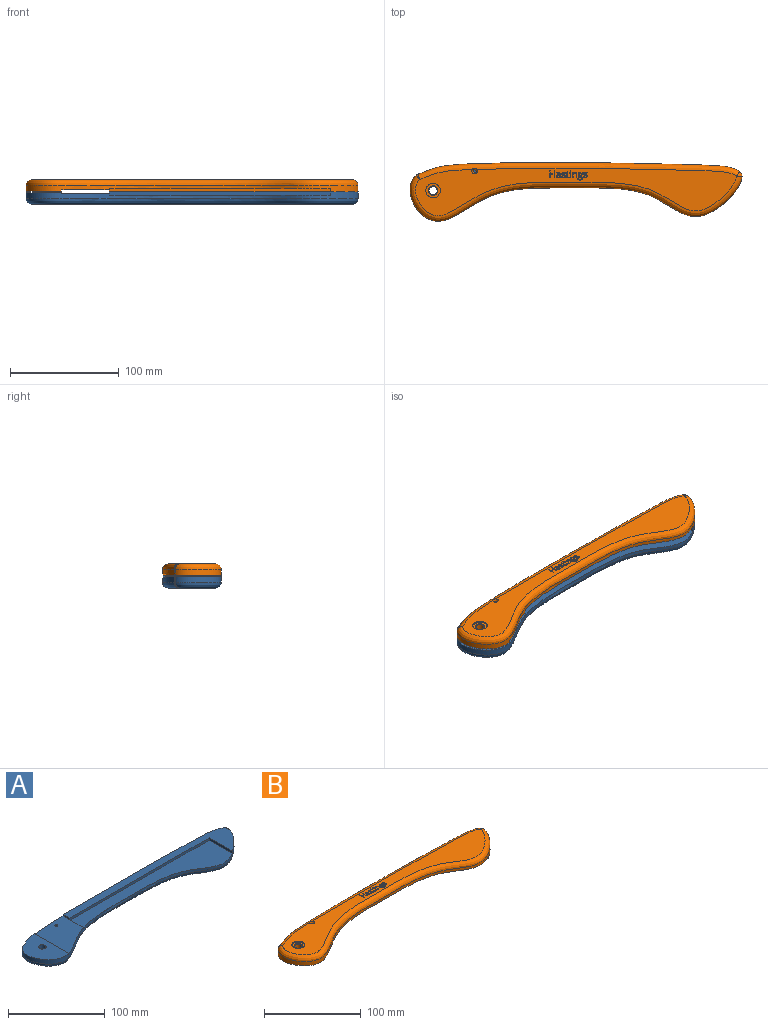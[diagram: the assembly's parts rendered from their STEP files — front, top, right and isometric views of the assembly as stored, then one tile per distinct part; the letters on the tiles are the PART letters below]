
ASSEMBLY  parts=2 mates=1
PART A: 28 faces, bbox 307.7x57.5x11.3 mm
  f0: cylinder r=3.81mm len=8.73mm, axis (0,0,-1), area 208.9mm2, adj f13,f26
  f1: cylinder r=5.08mm len=5.55mm, axis (0,0,-1), area 10.4mm2, adj f3,f6,f20,f26
  f2: cylinder r=1.52mm len=6.96mm, axis (0,0,-1), area 66.6mm2, adj f14,f25
  f3: extruded ~296.04x10.8mm, area 1751.2mm2, adj f1,f19,f22,f23,f24,f25,f26,f27
  f4: plane 19.58x1.24mm, normal (1,0,0), area 24.3mm2, adj f6,f15,f17,f25
  f5: plane 295.22x43.83mm, normal (0,0,-1), area 6249.9mm2, adj f7,f8,f9,f10,f11,f12,f14,f18
  f6: extruded ~305.25x42.05mm, area 1497.7mm2, adj f1,f4,f15,f16,f18,f19,f24,f25
  f7: plane 5.72x3.3mm, normal (-0.5,0.87,0), area 12.6mm2, adj f5,f8,f12,f13
  f8: plane 6.6x1.91mm, normal (-1,0,0), area 12.6mm2, adj f5,f7,f9,f13
  f9: plane 5.72x3.3mm, normal (-0.5,-0.87,0), area 12.6mm2, adj f5,f8,f10,f13
  f10: plane 5.72x3.3mm, normal (0.5,-0.87,0), area 12.6mm2, adj f5,f9,f11,f13
  f11: plane 6.6x1.91mm, normal (1,0,0), area 12.6mm2, adj f5,f10,f12,f13
  f12: plane 5.72x3.3mm, normal (0.5,0.87,0), area 12.6mm2, adj f5,f7,f11,f13
  f13: plane 13.2x11.43mm, normal (0,0,-1), area 67.5mm2, adj f0,f7,f8,f9,f10,f11,f12
  f14: cone r=2.54mm half-angle=21.8deg, axis (0,0,-1), area 34.9mm2, adj f2,f5,f22
  f15: plane 206.75x41.04mm, normal (0,0,1), area 3989.2mm2, adj f4,f6,f16,f17
  f16: plane 33.7x3.01mm, normal (-1,0,0), area 101.5mm2, adj f6,f15,f17,f27
  f17: plane 203.2x3.01mm, normal (0,-1,0), area 612.1mm2, adj f4,f15,f16,f23,f25,f27
  f18: bspline ~305.38x42.79mm, area 2862.2mm2, adj f5,f6,f20,f21
  f19: cylinder r=5.08mm len=6.19mm, axis (0,0,-1), area 31.9mm2, adj f3,f6,f21,f27
  f20: sphere r=5.08mm, area 9.5mm2, adj f1,f18,f22
  f21: sphere r=5.08mm, area 29.5mm2, adj f18,f19,f22
  f22: bspline ~296.04x15.55mm, area 2367.4mm2, adj f3,f5,f14,f20,f21
  f23: plane 9.75x1.77mm, normal (-1,0,0), area 17.3mm2, adj f3,f17,f25,f27
  f24: plane 49.96x1.14mm, normal (1,0,0), area 56.8mm2, adj f3,f6,f25,f26
  f25: plane 53.68x45.98mm, normal (0,0,1), area 1767.9mm2, adj f2,f3,f4,f6,f17,f23,f24
  f26: plane 52.52x34.33mm, normal (0,0,1), area 1250.7mm2, adj f0,f1,f3,f6,f24
  f27: plane 234.95x47.73mm, normal (0,0,1), area 2646.9mm2, adj f3,f6,f16,f17,f19,f23
PART B: 217 faces, bbox 307.7x57.5x11.1 mm
  f0: extruded ~296.04x10.8mm, area 1701.4mm2, adj f4,f5,f7,f17,f20,f21,f22,f216
  f1: extruded ~305.25x42.05mm, area 1469.7mm2, adj f2,f4,f7,f14,f15,f16,f20,f21
  f2: plane 33.7x2.85mm, normal (-1,0,0), area 96.2mm2, adj f1,f3,f14,f216
  f3: plane 203.2x2.85mm, normal (0,-1,0), area 579.7mm2, adj f2,f5,f14,f15,f21,f216
  f4: cylinder r=5.08mm len=6.03mm, axis (0,0,-1), area 31mm2, adj f0,f1,f19,f216
  f5: plane 9.75x1.81mm, normal (-1,0,0), area 17.6mm2, adj f0,f3,f21,f216
  f6: plane 295.22x43.83mm, normal (0,0,1), area 6146.7mm2, adj f10,f13,f16,f17,f23,f24,f25,f26
  f7: plane 49.96x1.15mm, normal (1,0,0), area 57.4mm2, adj f0,f1,f21,f22
  f8: cylinder r=3.81mm len=8.6mm, axis (0,0,-1), area 205.8mm2, adj f12,f22
  f9: cylinder r=1.52mm len=6.76mm, axis (0,0,-1), area 64.7mm2, adj f13,f21
  f10: cylinder r=6.64mm len=13.28mm, axis (0,0,1), area 56.2mm2, adj f6,f11
  f11: plane 13.28x13.28mm, normal (0,0,1), area 80mm2, adj f10,f12
  f12: cone r=3.81mm half-angle=45deg, axis (0,0,1), area 18.3mm2, adj f8,f11
  f13: cone r=1.52mm half-angle=21.8deg, axis (0,0,1), area 34.9mm2, adj f6,f9,f17
  f14: plane 206.75x41.04mm, normal (0,0,-1), area 3989.2mm2, adj f1,f2,f3,f15
  f15: plane 19.58x1.05mm, normal (1,0,0), area 20.5mm2, adj f1,f3,f14,f21
  f16: bspline ~305.38x42.79mm, area 2862.3mm2, adj f1,f6,f18,f19
  f17: bspline ~296.04x15.55mm, area 2367.3mm2, adj f0,f6,f13,f18,f19
  f18: sphere r=5.08mm, area 9.5mm2, adj f16,f17,f20
  f19: sphere r=5.08mm, area 29.5mm2, adj f4,f16,f17
  f20: cylinder r=5.08mm len=5.37mm, axis (0,0,-1), area 10mm2, adj f0,f1,f18,f22
  f21: plane 53.68x45.98mm, normal (0,0,-1), area 1767.9mm2, adj f0,f1,f3,f5,f7,f9,f15
  f22: plane 52.52x34.33mm, normal (0,0,-1), area 1250.7mm2, adj f0,f1,f7,f8,f20
  f23: extruded ~1.03x0.5mm, area 0.3mm2, adj f6,f24,f47,f48
  f24: extruded ~0.79x0.3mm, area 0.2mm2, adj f6,f23,f25,f48
  f25: extruded ~1.15x0.62mm, area 0.3mm2, adj f6,f24,f26,f48
  f26: extruded ~0.84x0.35mm, area 0.2mm2, adj f6,f25,f27,f48
  f27: extruded ~0.32x0.26mm, area 0.1mm2, adj f6,f26,f28,f48
  f28: extruded ~0.33x0.25mm, area 0.1mm2, adj f6,f27,f29,f48
  f29: extruded ~0.44x0.26mm, area 0.1mm2, adj f6,f28,f30,f48
  f30: extruded ~0.78x0.25mm, area 0.2mm2, adj f6,f29,f31,f48
  f31: extruded ~1.3x0.3mm, area 0.3mm2, adj f6,f30,f32,f48
  f32: plane 0.59x0.26mm, normal (-0.92,0.4,0), area 0.2mm2, adj f6,f31,f33,f48
  f33: extruded ~1.51x0.31mm, area 0.4mm2, adj f6,f32,f34,f48
  f34: extruded ~1.3x0.34mm, area 0.3mm2, adj f6,f33,f35,f48
  f35: extruded ~0.92x0.48mm, area 0.3mm2, adj f6,f34,f36,f48
  f36: extruded ~0.56x0.25mm, area 0.1mm2, adj f6,f35,f37,f48
  f37: extruded ~0.42x0.42mm, area 0.2mm2, adj f6,f36,f38,f48
  f38: extruded ~0.95x0.43mm, area 0.3mm2, adj f6,f37,f39,f48
  f39: extruded ~0.94x0.47mm, area 0.3mm2, adj f6,f38,f40,f48
  f40: extruded ~0.48x0.25mm, area 0.1mm2, adj f6,f39,f41,f48
  f41: extruded ~0.55x0.31mm, area 0.2mm2, adj f6,f40,f42,f48
  f42: extruded ~0.87x0.25mm, area 0.2mm2, adj f6,f41,f43,f48
  f43: extruded ~0.76x0.25mm, area 0.2mm2, adj f6,f42,f44,f48
  f44: extruded ~0.74x0.27mm, area 0.2mm2, adj f6,f43,f45,f48
  f45: plane 0.67x0.25mm, normal (1,0,0), area 0.2mm2, adj f6,f44,f46,f48
  f46: extruded ~1.48x0.3mm, area 0.4mm2, adj f6,f45,f47,f48
  f47: extruded ~1.4x0.36mm, area 0.4mm2, adj f6,f23,f46,f48
  f48: plane 4.95x3.39mm, normal (0,0,1), area 7mm2, adj f23,f24,f25,f26,f27,f28,f29,f30
  f49: extruded ~0.37x0.25mm, area 0.1mm2, adj f6,f50,f67,f68
  f50: extruded ~0.56x0.25mm, area 0.2mm2, adj f6,f49,f51,f68
  f51: extruded ~0.66x0.25mm, area 0.2mm2, adj f6,f50,f52,f68
  f52: plane 2.81x0.25mm, normal (-1,0,0), area 0.7mm2, adj f6,f51,f53,f68
  f53: plane 1.39x0.25mm, normal (0,1,0), area 0.4mm2, adj f6,f52,f54,f68
  f54: plane 0.56x0.25mm, normal (-1,0,0), area 0.1mm2, adj f6,f53,f55,f68
  f55: plane 1.39x0.25mm, normal (0,-1,0), area 0.4mm2, adj f6,f54,f56,f68
  f56: plane 1.11x0.25mm, normal (-1,0,0), area 0.3mm2, adj f6,f55,f57,f68
  f57: plane 0.42x0.25mm, normal (0,-1,0), area 0.1mm2, adj f6,f56,f58,f68
  f58: plane 1.02x0.3mm, normal (0.96,-0.29,0), area 0.3mm2, adj f6,f57,f59,f68
  f59: plane 0.69x0.3mm, normal (0.4,-0.92,0), area 0.2mm2, adj f6,f58,f60,f68
  f60: plane 0.35x0.25mm, normal (1,0,0), area 0.1mm2, adj f6,f59,f61,f68
  f61: plane 0.69x0.25mm, normal (0,1,0), area 0.2mm2, adj f6,f60,f62,f68
  f62: plane 2.84x0.25mm, normal (1,0,0), area 0.7mm2, adj f6,f61,f63,f68
  f63: extruded ~1.46x1.39mm, area 0.6mm2, adj f6,f62,f64,f68
  f64: extruded ~0.41x0.25mm, area 0.1mm2, adj f6,f63,f65,f68
  f65: extruded ~0.35x0.25mm, area 0.1mm2, adj f6,f64,f66,f68
  f66: plane 0.55x0.25mm, normal (-1,0,0), area 0.1mm2, adj f6,f65,f67,f68
  f67: extruded ~0.28x0.25mm, area 0.1mm2, adj f6,f49,f66,f68
  f68: plane 5.97x2.83mm, normal (0,0,1), area 5.9mm2, adj f49,f50,f51,f52,f53,f54,f55,f56
  f69: plane 0.72x0.25mm, normal (0,1,0), area 0.2mm2, adj f6,f70,f72,f73
  f70: plane 4.78x0.25mm, normal (-1,0,0), area 1.2mm2, adj f6,f69,f71,f73
  f71: plane 0.72x0.25mm, normal (0,-1,0), area 0.2mm2, adj f6,f70,f72,f73
  f72: plane 4.78x0.25mm, normal (1,0,0), area 1.2mm2, adj f6,f69,f71,f73
  f73: plane 4.78x0.72mm, normal (0,0,1), area 3.5mm2, adj f69,f70,f71,f72
  f74: extruded ~0.36x0.25mm, area 0.1mm2, adj f6,f75,f81,f82
  f75: extruded ~0.36x0.25mm, area 0.1mm2, adj f6,f74,f76,f82
  f76: extruded ~0.31x0.25mm, area 0.1mm2, adj f6,f75,f77,f82
  f77: extruded ~0.3x0.25mm, area 0.1mm2, adj f6,f76,f78,f82
  f78: extruded ~0.36x0.25mm, area 0.1mm2, adj f6,f77,f79,f82
  f79: extruded ~0.36x0.25mm, area 0.1mm2, adj f6,f78,f80,f82
  f80: extruded ~0.3x0.25mm, area 0.1mm2, adj f6,f79,f81,f82
  f81: extruded ~0.31x0.25mm, area 0.1mm2, adj f6,f74,f80,f82
  f82: plane 0.96x0.86mm, normal (0,0,1), area 0.7mm2, adj f74,f75,f76,f77,f78,f79,f80,f81
  f83: extruded ~0.76x0.28mm, area 0.2mm2, adj f84,f126,f127,f214
  f84: extruded ~0.82x0.28mm, area 0.2mm2, adj f83,f85,f127,f214
  f85: extruded ~0.79x0.27mm, area 0.2mm2, adj f84,f86,f127,f214
  f86: extruded ~1.08x1.07mm, area 0.4mm2, adj f85,f87,f127,f214
  f87: extruded ~1.06x1.03mm, area 0.4mm2, adj f86,f126,f127,f214
  f88: extruded ~0.59x0.33mm, area 0.2mm2, adj f89,f124,f127,f128
  f89: extruded ~0.68x0.28mm, area 0.2mm2, adj f88,f90,f127,f128
  f90: extruded ~0.77x0.25mm, area 0.2mm2, adj f89,f91,f127,f128
  f91: plane 0.87x0.25mm, normal (0,1,0), area 0.2mm2, adj f90,f92,f127,f128
  f92: extruded ~0.9x0.25mm, area 0.2mm2, adj f91,f93,f127,f128
  f93: extruded ~0.54x0.25mm, area 0.2mm2, adj f92,f94,f127,f128
  f94: extruded ~0.74x0.44mm, area 0.2mm2, adj f93,f95,f127,f128
  f95: extruded ~1.35x0.27mm, area 0.4mm2, adj f94,f124,f127,f128
  f96: plane 0.46x0.25mm, normal (-1,0,0), area 0.1mm2, adj f6,f97,f125,f127
  f97: plane 1.65x0.25mm, normal (0,-1,0), area 0.4mm2, adj f6,f96,f98,f127
  f98: extruded ~0.68x0.25mm, area 0.2mm2, adj f6,f97,f99,f127
  f99: extruded ~1.33x0.43mm, area 0.4mm2, adj f6,f98,f100,f127
  f100: extruded ~1.21x0.47mm, area 0.3mm2, adj f6,f99,f101,f127
  f101: extruded ~0.84x0.25mm, area 0.2mm2, adj f6,f100,f102,f127
  f102: extruded ~0.6x0.52mm, area 0.2mm2, adj f6,f101,f103,f127
  f103: extruded ~0.44x0.38mm, area 0.1mm2, adj f6,f102,f104,f127
  f104: extruded ~0.46x0.25mm, area 0.1mm2, adj f6,f103,f105,f127
  f105: extruded ~0.41x0.25mm, area 0.1mm2, adj f6,f104,f106,f127
  f106: extruded ~0.31x0.26mm, area 0.1mm2, adj f6,f105,f107,f127
  f107: extruded ~0.78x0.43mm, area 0.2mm2, adj f6,f106,f108,f127
  f108: extruded ~0.75x0.28mm, area 0.2mm2, adj f6,f107,f109,f127
  f109: extruded ~0.99x0.51mm, area 0.3mm2, adj f6,f108,f110,f127
  f110: extruded ~1.45x0.35mm, area 0.4mm2, adj f6,f109,f111,f127
  f111: extruded ~1.86x0.42mm, area 0.5mm2, adj f6,f110,f112,f127
  f112: extruded ~1.21x0.64mm, area 0.4mm2, adj f6,f111,f113,f127
  f113: extruded ~0.95x0.42mm, area 0.3mm2, adj f6,f112,f114,f127
  f114: extruded ~1.19x0.33mm, area 0.3mm2, adj f6,f113,f115,f127
  f115: plane 0.85x0.25mm, normal (0,-1,0), area 0.2mm2, adj f6,f114,f116,f127
  f116: extruded ~0.55x0.25mm, area 0.1mm2, adj f6,f115,f117,f127
  f117: extruded ~0.29x0.25mm, area 0.1mm2, adj f6,f116,f118,f127
  f118: extruded ~0.61x0.46mm, area 0.2mm2, adj f6,f117,f119,f127
  f119: extruded ~0.4x0.25mm, area 0.1mm2, adj f6,f118,f120,f127
  f120: extruded ~1.32x0.42mm, area 0.4mm2, adj f6,f119,f121,f127
  f121: extruded ~1.12x0.48mm, area 0.3mm2, adj f6,f120,f122,f127
  f122: extruded ~0.56x0.25mm, area 0.1mm2, adj f6,f121,f123,f127
  f123: extruded ~0.4x0.25mm, area 0.1mm2, adj f6,f122,f125,f127
  f124: extruded ~0.94x0.25mm, area 0.2mm2, adj f88,f95,f127,f128
  f125: plane 0.88x0.25mm, normal (-0.12,0.99,0), area 0.2mm2, adj f6,f96,f123,f127
  f126: extruded ~0.79x0.26mm, area 0.2mm2, adj f83,f87,f127,f214
  f127: plane 7.01x4.51mm, normal (0,0,1), area 13.1mm2, adj f83,f84,f85,f86,f87,f88,f89,f90
  f128: plane 3.05x1.7mm, normal (0,0,1), area 4.4mm2, adj f88,f89,f90,f91,f92,f93,f94,f95
  f129: extruded ~1.06x0.37mm, area 0.3mm2, adj f130,f155,f156,f215
  f130: extruded ~0.66x0.25mm, area 0.2mm2, adj f129,f131,f156,f215
  f131: extruded ~0.6x0.25mm, area 0.2mm2, adj f130,f132,f156,f215
  f132: extruded ~0.74x0.38mm, area 0.2mm2, adj f131,f133,f156,f215
  f133: extruded ~1.24x0.27mm, area 0.3mm2, adj f132,f134,f156,f215
  f134: plane 0.72x0.25mm, normal (-0.04,1,0), area 0.2mm2, adj f133,f135,f156,f215
  f135: plane 0.43x0.25mm, normal (1,0,0), area 0.1mm2, adj f134,f155,f156,f215
  f136: plane 0.68x0.25mm, normal (0.98,0.21,0), area 0.2mm2, adj f6,f137,f154,f156
  f137: plane 0.54x0.25mm, normal (0,1,0), area 0.1mm2, adj f6,f136,f138,f156
  f138: plane 3.26x0.25mm, normal (-1,0,0), area 0.8mm2, adj f6,f137,f139,f156
  f139: extruded ~1.22x0.41mm, area 0.3mm2, adj f6,f138,f140,f156
  f140: extruded ~1.27x0.38mm, area 0.3mm2, adj f6,f139,f141,f156
  f141: extruded ~0.84x0.25mm, area 0.2mm2, adj f6,f140,f142,f156
  f142: extruded ~0.77x0.3mm, area 0.2mm2, adj f6,f141,f143,f156
  f143: plane 0.55x0.25mm, normal (0.93,0.37,0), area 0.2mm2, adj f6,f142,f144,f156
  f144: extruded ~1.35x0.37mm, area 0.4mm2, adj f6,f143,f145,f156
  f145: extruded ~0.77x0.27mm, area 0.2mm2, adj f6,f144,f146,f156
  f146: extruded ~0.83x0.25mm, area 0.2mm2, adj f6,f145,f147,f156
  f147: plane 0.3x0.25mm, normal (1,0,0), area 0.1mm2, adj f6,f146,f148,f156
  f148: plane 0.81x0.25mm, normal (0.03,-1,0), area 0.2mm2, adj f6,f147,f149,f156
  f149: extruded ~2.31x1.52mm, area 0.8mm2, adj f6,f148,f150,f156
  f150: extruded ~1.04x0.4mm, area 0.3mm2, adj f6,f149,f151,f156
  f151: extruded ~1.11x0.37mm, area 0.3mm2, adj f6,f150,f152,f156
  f152: extruded ~0.89x0.25mm, area 0.2mm2, adj f6,f151,f153,f156
  f153: extruded ~0.71x0.61mm, area 0.2mm2, adj f6,f152,f154,f156
  f154: plane 0.25x0.04mm, normal (0,1,0), area 0mm2, adj f6,f136,f153,f156
  f155: extruded ~1.04x0.39mm, area 0.3mm2, adj f129,f135,f156,f215
  f156: plane 4.94x3.83mm, normal (0,0,1), area 8.9mm2, adj f129,f130,f131,f132,f133,f134,f135,f136
  f157: extruded ~1.03x0.5mm, area 0.3mm2, adj f6,f158,f181,f182
  f158: extruded ~0.79x0.3mm, area 0.2mm2, adj f6,f157,f159,f182
  f159: extruded ~1.15x0.62mm, area 0.3mm2, adj f6,f158,f160,f182
  f160: extruded ~0.84x0.35mm, area 0.2mm2, adj f6,f159,f161,f182
  f161: extruded ~0.32x0.26mm, area 0.1mm2, adj f6,f160,f162,f182
  f162: extruded ~0.33x0.25mm, area 0.1mm2, adj f6,f161,f163,f182
  f163: extruded ~0.44x0.26mm, area 0.1mm2, adj f6,f162,f164,f182
  f164: extruded ~0.78x0.25mm, area 0.2mm2, adj f6,f163,f165,f182
  f165: extruded ~1.3x0.3mm, area 0.3mm2, adj f6,f164,f166,f182
  f166: plane 0.59x0.26mm, normal (-0.92,0.4,0), area 0.2mm2, adj f6,f165,f167,f182
  f167: extruded ~1.51x0.31mm, area 0.4mm2, adj f6,f166,f168,f182
  f168: extruded ~1.3x0.34mm, area 0.3mm2, adj f6,f167,f169,f182
  f169: extruded ~0.92x0.48mm, area 0.3mm2, adj f6,f168,f170,f182
  f170: extruded ~0.56x0.25mm, area 0.1mm2, adj f6,f169,f171,f182
  f171: extruded ~0.42x0.42mm, area 0.2mm2, adj f6,f170,f172,f182
  f172: extruded ~0.95x0.43mm, area 0.3mm2, adj f6,f171,f173,f182
  f173: extruded ~0.94x0.47mm, area 0.3mm2, adj f6,f172,f174,f182
  f174: extruded ~0.48x0.25mm, area 0.1mm2, adj f6,f173,f175,f182
  f175: extruded ~0.55x0.31mm, area 0.2mm2, adj f6,f174,f176,f182
  f176: extruded ~0.87x0.25mm, area 0.2mm2, adj f6,f175,f177,f182
  f177: extruded ~0.76x0.25mm, area 0.2mm2, adj f6,f176,f178,f182
  f178: extruded ~0.74x0.27mm, area 0.2mm2, adj f6,f177,f179,f182
  f179: plane 0.67x0.25mm, normal (1,0,0), area 0.2mm2, adj f6,f178,f180,f182
  f180: extruded ~1.48x0.3mm, area 0.4mm2, adj f6,f179,f181,f182
  f181: extruded ~1.4x0.36mm, area 0.4mm2, adj f6,f157,f180,f182
  f182: plane 4.95x3.39mm, normal (0,0,1), area 7mm2, adj f157,f158,f159,f160,f161,f162,f163,f164
  f183: plane 3.09x0.25mm, normal (1,0,0), area 0.8mm2, adj f6,f184,f199,f200
  f184: plane 0.72x0.25mm, normal (0,1,0), area 0.2mm2, adj f6,f183,f185,f200
  f185: plane 3.12x0.25mm, normal (-1,0,0), area 0.8mm2, adj f6,f184,f186,f200
  f186: extruded ~1.33x0.44mm, area 0.4mm2, adj f6,f185,f187,f200
  f187: extruded ~1.3x0.42mm, area 0.4mm2, adj f6,f186,f188,f200
  f188: extruded ~0.89x0.25mm, area 0.2mm2, adj f6,f187,f189,f200
  f189: extruded ~0.62x0.55mm, area 0.2mm2, adj f6,f188,f190,f200
  f190: plane 0.25x0.04mm, normal (0,-1,0), area 0mm2, adj f6,f189,f191,f200
  f191: plane 0.65x0.25mm, normal (-0.98,-0.18,0), area 0.2mm2, adj f6,f190,f192,f200
  f192: plane 0.59x0.25mm, normal (0,-1,0), area 0.1mm2, adj f6,f191,f193,f200
  f193: plane 4.78x0.25mm, normal (1,0,0), area 1.2mm2, adj f6,f192,f194,f200
  f194: plane 0.72x0.25mm, normal (0,1,0), area 0.2mm2, adj f6,f193,f195,f200
  f195: plane 2.51x0.25mm, normal (-1,0,0), area 0.6mm2, adj f6,f194,f196,f200
  f196: extruded ~1.34x0.35mm, area 0.4mm2, adj f6,f195,f197,f200
  f197: extruded ~1.1x0.41mm, area 0.3mm2, adj f6,f196,f198,f200
  f198: extruded ~0.83x0.29mm, area 0.2mm2, adj f6,f197,f199,f200
  f199: extruded ~0.87x0.27mm, area 0.2mm2, adj f6,f183,f198,f200
  f200: plane 4.87x3.99mm, normal (0,0,1), area 8.3mm2, adj f183,f184,f185,f186,f187,f188,f189,f190
  f201: plane 0.74x0.25mm, normal (0,1,0), area 0.2mm2, adj f6,f202,f212,f213
  f202: plane 6.37x0.25mm, normal (-1,0,0), area 1.6mm2, adj f6,f201,f203,f213
  f203: plane 0.74x0.25mm, normal (0,-1,0), area 0.2mm2, adj f6,f202,f204,f213
  f204: plane 2.71x0.25mm, normal (1,0,0), area 0.7mm2, adj f6,f203,f205,f213
  f205: plane 3.36x0.25mm, normal (0,-1,0), area 0.9mm2, adj f6,f204,f206,f213
  f206: plane 2.71x0.25mm, normal (-1,0,0), area 0.7mm2, adj f6,f205,f207,f213
  f207: plane 0.74x0.25mm, normal (0,-1,0), area 0.2mm2, adj f6,f206,f208,f213
  f208: plane 6.37x0.25mm, normal (1,0,0), area 1.6mm2, adj f6,f207,f209,f213
  f209: plane 0.74x0.25mm, normal (0,1,0), area 0.2mm2, adj f6,f208,f210,f213
  f210: plane 3x0.25mm, normal (-1,0,0), area 0.8mm2, adj f6,f209,f211,f213
  f211: plane 3.36x0.25mm, normal (0,1,0), area 0.9mm2, adj f6,f210,f212,f213
  f212: plane 3x0.25mm, normal (1,0,0), area 0.8mm2, adj f6,f201,f211,f213
  f213: plane 6.37x4.84mm, normal (0,0,1), area 11.7mm2, adj f201,f202,f203,f204,f205,f206,f207,f208
  f214: plane 2.13x2.11mm, normal (0,0,1), area 3.7mm2, adj f83,f84,f85,f86,f87,f126
  f215: plane 2.35x1.84mm, normal (0,0,1), area 3.5mm2, adj f129,f130,f131,f132,f133,f134,f135,f155
  f216: plane 234.95x47.73mm, normal (0,0,-1), area 2646.9mm2, adj f0,f1,f2,f3,f4,f5
PLACE A t=(-70.22,-42,-1.87)mm
PLACE B t=(-70.22,-42,-1.85)mm
MATE fastened B.f216 <-> A.f27  axis (0,0,-1) through (-16.98,-28.34,9.4)mm
